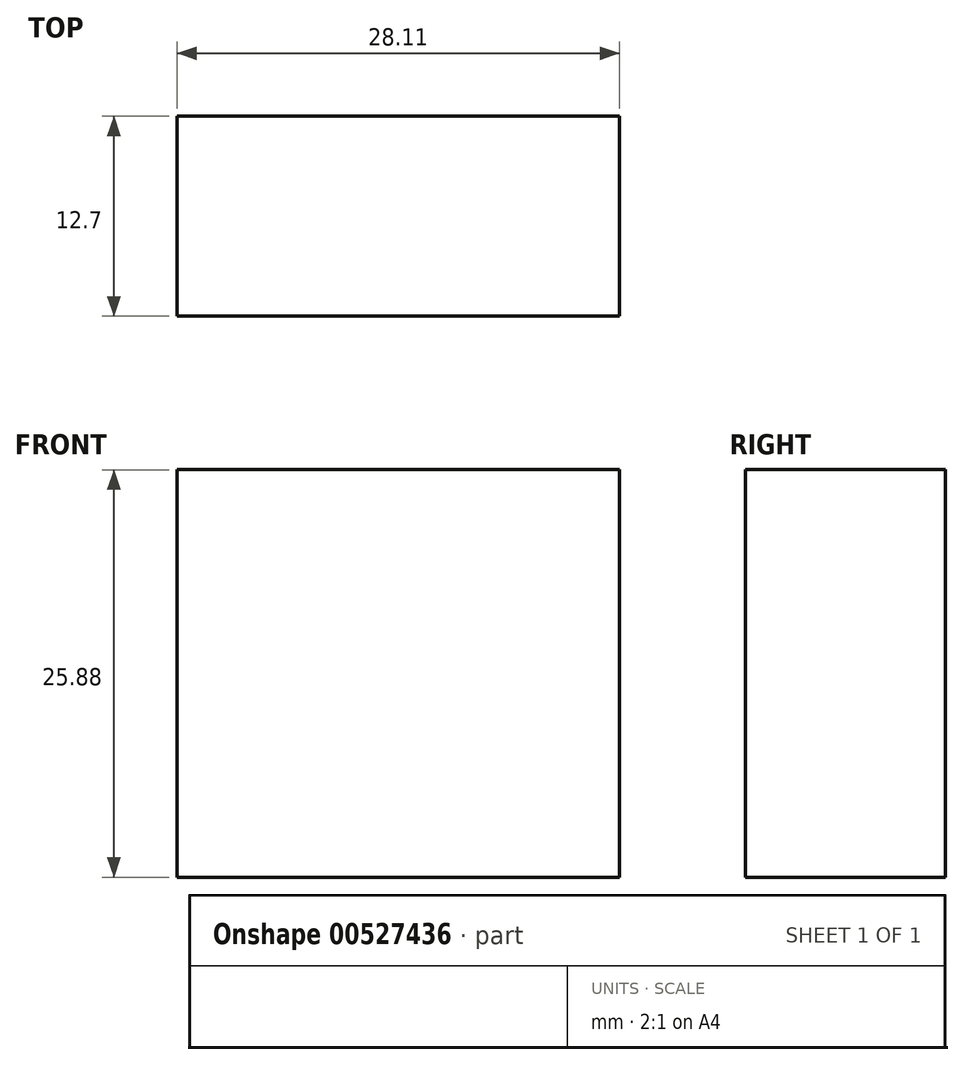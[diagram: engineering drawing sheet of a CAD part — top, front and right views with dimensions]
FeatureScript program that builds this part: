
annotation { "Feature Type Name" : "Feature", "Feature Type Description" : "" }
export const myFeature = defineFeature(function(context is Context, id is Id, definition is map)
    precondition{}
    {
        {
            var Q0;
            Q0=qCreatedBy(makeId("Front.planeOp"),FACE);
            var sketch = newSketch(context, id + "F0", { "sketchPlane" : qUnion([Q0])});
            skLineSegment(sketch, "E0.bottom", {"start": v(-116.9, 58.56) * mm, "end": v(-88.8, 58.56) * mm});
            skLineSegment(sketch, "E0.top", {"start": v(-116.9, 32.68) * mm, "end": v(-88.8, 32.68) * mm});
            skLineSegment(sketch, "E0.left", {"start": v(-116.9, 58.56) * mm, "end": v(-116.9, 32.68) * mm});
            skLineSegment(sketch, "E0.right", {"start": v(-88.8, 58.56) * mm, "end": v(-88.8, 32.68) * mm});
            skSolve(sketch);
        }
        {
            var Q0;
            Q0 = qSketchRegion(id + "F0", true);
            extrude(context, id + "F1", {"entities" : qUnion([Q0]), "depth" : 12.7 * mm, "offsetDistance" : 25.4 * mm});
        }
    });
